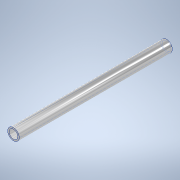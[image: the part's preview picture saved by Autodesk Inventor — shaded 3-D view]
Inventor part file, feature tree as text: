
AUTODESK INVENTOR PART (.ipt)
format: ipt  version: 2020.3 (Build 243373000, 373)  size: 98,816 bytes
history: native  units: mm
features: other x1, extrude x1, sketch x1
ambient origin geometry x8: Origin, YZ Plane, XZ Plane, XY Plane, X Axis, Y Axis, Z Axis, Center Point
bodies: Body1 (feature_tree)
feature tree (3):
  other  "ソリッド1"
  extrude  "押し出し1"  Depth=4.0mm
  sketch  "スケッチ1"
